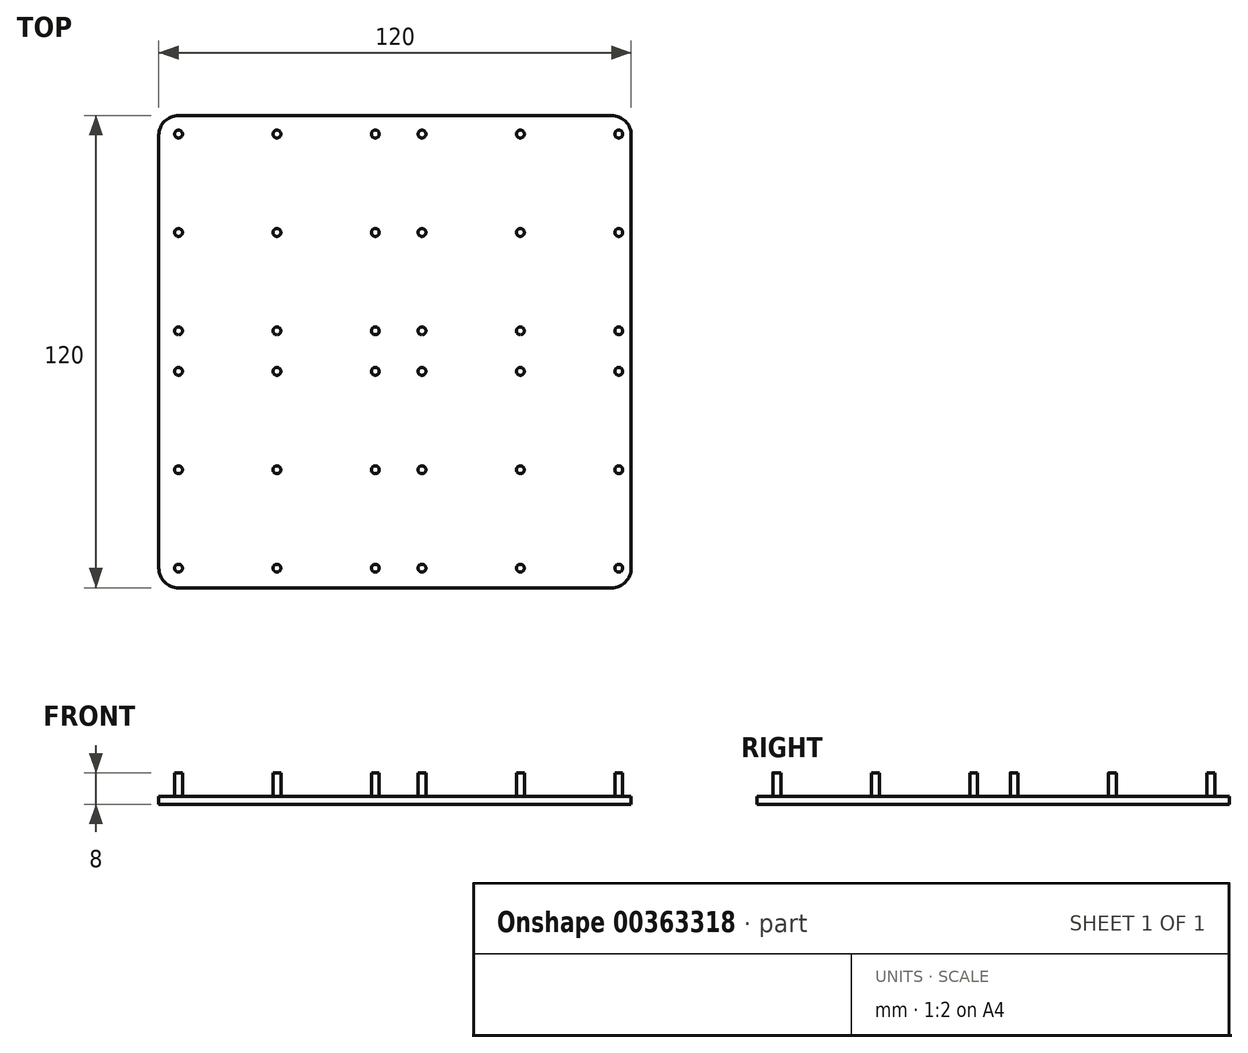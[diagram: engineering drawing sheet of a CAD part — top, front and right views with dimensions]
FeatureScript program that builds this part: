
annotation { "Feature Type Name" : "Feature", "Feature Type Description" : "" }
export const myFeature = defineFeature(function(context is Context, id is Id, definition is map)
    precondition{}
    {
        {
            var Q0;
            Q0=qCreatedBy(makeId("Top.planeOp"),FACE);
            var sketch = newSketch(context, id + "F0", { "sketchPlane" : qUnion([Q0])});
            skLineSegment(sketch, "E0.bottom", {"start": v(59.08, 59.85) * mm, "end": v(-60.92, 59.85) * mm});
            skLineSegment(sketch, "E0.top", {"start": v(59.08, -60.15) * mm, "end": v(-60.92, -60.15) * mm});
            skLineSegment(sketch, "E0.left", {"start": v(59.08, 59.85) * mm, "end": v(59.08, -60.15) * mm});
            skLineSegment(sketch, "E0.right", {"start": v(-60.92, 59.85) * mm, "end": v(-60.92, -60.15) * mm});
            skPoint(sketch, "E0.middle", {"position": v(-0.92, -0.15) * mm});
            skSolve(sketch);
        }
        {
            var Q0;
            Q0 = qSketchRegion(id + "F0", true);
            extrude(context, id + "F1", {"entities" : qUnion([Q0]), "depth" : 2 * mm});
        }
        {
            var Q0;
            Q0=makeQuery(id+"F1.opExtrude","SWEPT_EDGE",EDGE,{"disambiguationData":[OSD([sQuery(id+"F0.wireOp",EDGE,"E0.top"),sQuery(id+"F0.wireOp",EDGE,"E0.left")])]});
            var Q1;
            Q1=makeQuery(id+"F1.opExtrude","SWEPT_EDGE",EDGE,{"disambiguationData":[OSD([sQuery(id+"F0.wireOp",EDGE,"E0.bottom"),sQuery(id+"F0.wireOp",EDGE,"E0.left")])]});
            var Q2;
            Q2=makeQuery(id+"F1.opExtrude","SWEPT_EDGE",EDGE,{"disambiguationData":[OSD([sQuery(id+"F0.wireOp",EDGE,"E0.bottom"),sQuery(id+"F0.wireOp",EDGE,"E0.right")])]});
            var Q3;
            Q3=makeQuery(id+"F1.opExtrude","SWEPT_EDGE",EDGE,{"disambiguationData":[OSD([sQuery(id+"F0.wireOp",EDGE,"E0.top"),sQuery(id+"F0.wireOp",EDGE,"E0.right")])]});
            fillet(context, id + "F2", {"entities" : qUnion([Q0, Q1, Q2, Q3]), "radius" : 5 * mm, "tangentPropagation" : true, "allowEdgeOverflow" : false});
        }
        {
            var Q0;
            Q0=makeQuery(id+"F1.opExtrude","CAP_FACE",FACE,{"disambiguationData":[OSD([sQuery(id+"F0.wireOp",EDGE,"E0.bottom"),sQuery(id+"F0.wireOp",EDGE,"E0.top"),sQuery(id+"F0.wireOp",EDGE,"E0.left"),sQuery(id+"F0.wireOp",EDGE,"E0.right")])],"isStart":false});
            var sketch = newSketch(context, id + "F3", { "sketchPlane" : qUnion([Q0])});
            skCircle(sketch, "E1", {"center": v(-55.92, -55.15) * mm, "radius": 1 * mm});
            skCircle(sketch, "E2.0.1.0", {"center": v(-55.92, -30.15) * mm, "radius": 1 * mm});
            skCircle(sketch, "E2.1.0.0", {"center": v(-30.92, -55.15) * mm, "radius": 1 * mm});
            skCircle(sketch, "E2.1.1.0", {"center": v(-30.92, -30.15) * mm, "radius": 1 * mm});
            skCircle(sketch, "E2.2.0.0", {"center": v(-5.92, -55.15) * mm, "radius": 1 * mm});
            skCircle(sketch, "E2.2.1.0", {"center": v(-5.92, -30.15) * mm, "radius": 1 * mm});
            skLineSegment(sketch, "E2.direction1", {"start": v(-55.92, -55.15) * mm, "end": v(-30.92, -55.15) * mm, "construction": true});
            skLineSegment(sketch, "E2.direction2", {"start": v(-55.92, -55.15) * mm, "end": v(-55.92, -30.15) * mm, "construction": true});
            skCircle(sketch, "E3.0.0.2", {"center": v(-55.92, -5.15) * mm, "radius": 1 * mm});
            skCircle(sketch, "E3.0.1.2", {"center": v(-30.92, -5.15) * mm, "radius": 1 * mm});
            skCircle(sketch, "E3.0.2.2", {"center": v(-5.92, -5.15) * mm, "radius": 1 * mm});
            skCircle(sketch, "E4.MirrorC", {"center": v(5.92, -30.15) * mm, "radius": 1 * mm});
            skCircle(sketch, "E5.MirrorC", {"center": v(5.92, -55.15) * mm, "radius": 1 * mm});
            skCircle(sketch, "E6.MirrorC", {"center": v(5.92, -5.15) * mm, "radius": 1 * mm});
            skCircle(sketch, "E7.MirrorC", {"center": v(30.92, -5.15) * mm, "radius": 1 * mm});
            skCircle(sketch, "E8.MirrorC", {"center": v(55.92, -5.15) * mm, "radius": 1 * mm});
            skCircle(sketch, "E9.MirrorC", {"center": v(55.92, -30.15) * mm, "radius": 1 * mm});
            skCircle(sketch, "E10.MirrorC", {"center": v(55.92, -55.15) * mm, "radius": 1 * mm});
            skCircle(sketch, "E11.MirrorC", {"center": v(30.92, -55.15) * mm, "radius": 1 * mm});
            skCircle(sketch, "E12.MirrorC", {"center": v(30.92, -30.15) * mm, "radius": 1 * mm});
            skCircle(sketch, "E13.MirrorC", {"center": v(-55.92, 5.15) * mm, "radius": 1 * mm});
            skCircle(sketch, "E14.MirrorC", {"center": v(-30.92, 5.15) * mm, "radius": 1 * mm});
            skCircle(sketch, "E15.MirrorC", {"center": v(-5.92, 5.15) * mm, "radius": 1 * mm});
            skCircle(sketch, "E16.MirrorC", {"center": v(5.92, 5.15) * mm, "radius": 1 * mm});
            skCircle(sketch, "E17.MirrorC", {"center": v(30.92, 5.15) * mm, "radius": 1 * mm});
            skCircle(sketch, "E18.MirrorC", {"center": v(55.92, 5.15) * mm, "radius": 1 * mm});
            skCircle(sketch, "E19.MirrorC", {"center": v(-55.92, 30.15) * mm, "radius": 1 * mm});
            skCircle(sketch, "E20.MirrorC", {"center": v(-30.92, 30.15) * mm, "radius": 1 * mm});
            skCircle(sketch, "E21.MirrorC", {"center": v(5.92, 30.15) * mm, "radius": 1 * mm});
            skCircle(sketch, "E22.MirrorC", {"center": v(-5.92, 30.15) * mm, "radius": 1 * mm});
            skCircle(sketch, "E23.MirrorC", {"center": v(30.92, 30.15) * mm, "radius": 1 * mm});
            skCircle(sketch, "E24.MirrorC", {"center": v(55.92, 30.15) * mm, "radius": 1 * mm});
            skCircle(sketch, "E25.MirrorC", {"center": v(55.92, 55.15) * mm, "radius": 1 * mm});
            skCircle(sketch, "E26.MirrorC", {"center": v(5.92, 55.15) * mm, "radius": 1 * mm});
            skCircle(sketch, "E27.MirrorC", {"center": v(-5.92, 55.15) * mm, "radius": 1 * mm});
            skCircle(sketch, "E28.MirrorC", {"center": v(-30.92, 55.15) * mm, "radius": 1 * mm});
            skCircle(sketch, "E29.MirrorC", {"center": v(-55.92, 55.15) * mm, "radius": 1 * mm});
            skCircle(sketch, "E30.MirrorC", {"center": v(30.92, 55.15) * mm, "radius": 1 * mm});
            skSolve(sketch);
        }
        {
            var Q0;
            Q0 = qSketchRegion(id + "F3", true);
            extrude(context, id + "F4", {"entities" : qUnion([Q0]), "operationType" : NewBodyOperationType.ADD, "offsetDistance" : 25 * mm, "depth" : 6 * mm});
        }
    });
